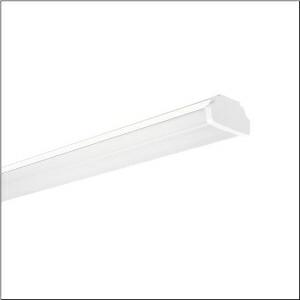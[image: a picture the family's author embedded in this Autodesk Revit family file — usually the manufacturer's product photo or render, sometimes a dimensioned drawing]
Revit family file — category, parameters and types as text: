
# Revit family: modario_31_gen_2_53bm812mv4g5d2_cdf0
name_source: partatom
category: Lighting Fixtures
units: mm (PartAtom-declared; Revit-internal decimal feet)

## family parameters
Cut with Voids When Loaded = No
Host = Face
Light Source = No
Part Type = Normal
Room Calculation Point = No
Round Connector Dimension = Use Diameter
Shared = No

## types (1)
- --- (1 x LED, 16690 lm, 89.8 W, 4000K)
    Apparent Load = 90 VA
    CIE Flux Codes = 47 80 95 93 100
    Color Rendering = 80
    Color Temperature = 4000K
    Default Elevation = 1800 mm
    Description = Modario 31 Gen.2, luminaire insert, of sheet steel, coil coated, white, length: 1.495mm, width: 81mm, height: 82mm, 5x system unit, system units: 299mm, LED rated luminous flux: 16.690lm, light colour: 840, SDCM (Standard Deviation of Colour Matching)MacAdam ≤ 3 SDCM (initial), control gear: ON/OFF Multilumen, control gear: ECG, with plug, 3-pole, with phase selection, mains connection: 220..240V, AC, 50/60Hz, rated input power: 90W, through-wiring accessed according to module size, primary optical cover: cover, of PMMA, light emission: direct distribution, primary light characteristic: symmetric, protection rating (complete): IP20, protection rating (LED compartment): IP50, insulation class (complete): insulation class I (protective earthing), certification: CE, ENEC, VDE, UKCA, impact resistance: IK03, permissible ambient temperature for indoor applications: -35..+30°C, corresponds to IFS (International Featured Standards) requirements for safety and quality in the food industry, reducing of maximum allowable ambient temperature of 5°C with ceiling mounting, IP40 when using the optional accessory 5TP9018, packaging unit: 1 piece
    Height = 92 mm
    Lamp = 1 x LED
    Lamp Light Flux = 16690 lm
    Lamp Power = 89.8 W
    Lamp count = 1
    Length = 1495 mm
    Luminous efficacy = 186 lm/W
    Manufacturer = Siteco
    ModVariant = No
    Model = 53BM812MV4G5D2
    Mounting Place = Ceiling
    Mounting Type = Pendant
    Number of Poles = 1
    OnlyDefault = Yes
    Power Factor = 1
    Product Name = Modario 31 Gen.2
    Product group = luminaire insert | ceiling pendant
    ProductGroupID = 901
    Protection Class = Protection class I
    Protection Degree = IP 20
    RLX_Detail_Level = 1
    RLX_Emergency_Light_Flux = 0 lm
    RLX_Emergency_Type = 0
    RLX_Emergency_Type_DB = No
    RlxData = <blob elided: 40013 chars, md5=487cc29e>
    Socket = socket
    Standby Power = 0 W
    System Light Flux = 16690 lm
    System Power = 90 W
    Type Comments = factory setting: luminous flux: 100 % | (A | C | E) | 210 mA
    Type Image = l_1341886.jpg
    URL = http://relux.com
    VarID = @adj_050801
    Voltage = 0 V
    Weight = 0.00 kg
    Width = 81 mm

## geometry (parser evidence)
native form markers: Blend x4, Sweep x12
no freeform markers — native parametric forms only
